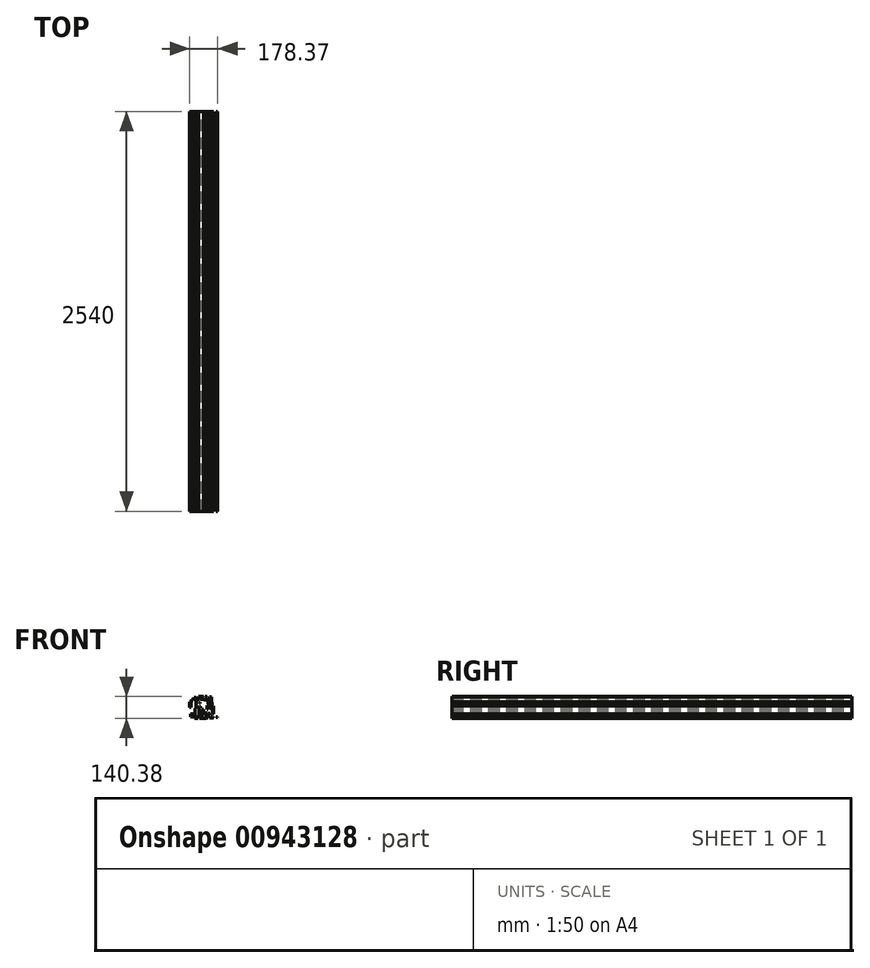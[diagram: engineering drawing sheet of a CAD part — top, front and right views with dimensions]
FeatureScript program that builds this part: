
annotation { "Feature Type Name" : "Feature", "Feature Type Description" : "" }
export const myFeature = defineFeature(function(context is Context, id is Id, definition is map)
    precondition{}
    {
        {
            var Q0;
            Q0=qCreatedBy(makeId("Front.planeOp"),FACE);
            var sketch = newSketch(context, id + "F0", { "sketchPlane" : qUnion([Q0])});
            skLineSegment(sketch, "E0.bottom", {"start": v(-67.4, -14.84) * mm, "end": v(-42.91, -14.84) * mm});
            skLineSegment(sketch, "E0.top", {"start": v(-67.4, -67.62) * mm, "end": v(-42.91, -67.62) * mm});
            skLineSegment(sketch, "E0.left", {"start": v(-67.4, -14.84) * mm, "end": v(-67.4, -67.62) * mm});
            skLineSegment(sketch, "E0.right", {"start": v(-42.91, -14.84) * mm, "end": v(-42.91, -67.62) * mm});
            skLineSegment(sketch, "E1.bottom", {"start": v(9.7, -18.66) * mm, "end": v(14, -18.66) * mm});
            skLineSegment(sketch, "E1.top", {"start": v(9.7, 7.1) * mm, "end": v(14, 7.1) * mm});
            skLineSegment(sketch, "E1.left", {"start": v(9.7, -18.66) * mm, "end": v(9.7, 7.1) * mm});
            skLineSegment(sketch, "E1.right", {"start": v(14, -18.66) * mm, "end": v(14, 7.1) * mm});
            skLineSegment(sketch, "E2.bottom", {"start": v(-19.39, 24.1) * mm, "end": v(-22.09, 24.1) * mm});
            skLineSegment(sketch, "E2.top", {"start": v(-19.39, 24.1) * mm, "end": v(-22.09, 24.1) * mm});
            skLineSegment(sketch, "E2.left", {"start": v(-19.39, 24.1) * mm, "end": v(-19.39, 24.1) * mm});
            skLineSegment(sketch, "E2.right", {"start": v(-22.09, 24.1) * mm, "end": v(-22.09, 24.1) * mm});
            skLineSegment(sketch, "E3.bottom", {"start": v(-36.08, 23.15) * mm, "end": v(-39.73, 23.15) * mm});
            skLineSegment(sketch, "E3.top", {"start": v(-36.08, 17.59) * mm, "end": v(-39.73, 17.59) * mm});
            skLineSegment(sketch, "E3.left", {"start": v(-36.08, 23.15) * mm, "end": v(-36.08, 17.59) * mm});
            skLineSegment(sketch, "E3.right", {"start": v(-39.73, 23.15) * mm, "end": v(-39.73, 17.59) * mm});
            skLineSegment(sketch, "E4.bottom", {"start": v(-38.14, -1.65) * mm, "end": v(-33.7, -1.65) * mm});
            skLineSegment(sketch, "E4.top", {"start": v(-38.14, -9.91) * mm, "end": v(-33.7, -9.91) * mm});
            skLineSegment(sketch, "E4.left", {"start": v(-38.14, -1.65) * mm, "end": v(-38.14, -9.91) * mm});
            skLineSegment(sketch, "E4.right", {"start": v(-33.7, -1.65) * mm, "end": v(-33.7, -9.91) * mm});
            skLineSegment(sketch, "E5.bottom", {"start": v(-27.18, -19.3) * mm, "end": v(-14.3, -19.3) * mm});
            skLineSegment(sketch, "E5.top", {"start": v(-27.18, -38.21) * mm, "end": v(-14.3, -38.21) * mm});
            skLineSegment(sketch, "E5.left", {"start": v(-27.18, -19.3) * mm, "end": v(-27.18, -38.21) * mm});
            skLineSegment(sketch, "E5.right", {"start": v(-14.3, -19.3) * mm, "end": v(-14.3, -38.21) * mm});
            skLineSegment(sketch, "E6.bottom", {"start": v(-6.5, -42.98) * mm, "end": v(7.8, -42.98) * mm});
            skLineSegment(sketch, "E6.top", {"start": v(-6.5, -53.32) * mm, "end": v(7.8, -53.32) * mm});
            skLineSegment(sketch, "E6.left", {"start": v(-6.5, -42.98) * mm, "end": v(-6.5, -53.32) * mm});
            skLineSegment(sketch, "E6.right", {"start": v(7.8, -42.98) * mm, "end": v(7.8, -53.32) * mm});
            skLineSegment(sketch, "E7.bottom", {"start": v(14, -54.59) * mm, "end": v(25.92, -54.59) * mm});
            skLineSegment(sketch, "E7.top", {"start": v(14, -45.53) * mm, "end": v(25.92, -45.53) * mm});
            skLineSegment(sketch, "E7.left", {"start": v(14, -54.59) * mm, "end": v(14, -45.53) * mm});
            skLineSegment(sketch, "E7.right", {"start": v(25.92, -54.59) * mm, "end": v(25.92, -45.53) * mm});
            skLineSegment(sketch, "E8.bottom", {"start": v(33.24, -13.25) * mm, "end": v(26.56, -13.25) * mm});
            skLineSegment(sketch, "E8.top", {"start": v(33.24, 9.96) * mm, "end": v(26.56, 9.96) * mm});
            skLineSegment(sketch, "E8.left", {"start": v(33.24, -13.25) * mm, "end": v(33.24, 9.96) * mm});
            skLineSegment(sketch, "E8.right", {"start": v(26.56, -13.25) * mm, "end": v(26.56, 9.96) * mm});
            skLineSegment(sketch, "E9.bottom", {"start": v(23.86, 16) * mm, "end": v(14.95, 16) * mm});
            skLineSegment(sketch, "E9.top", {"start": v(23.86, 36.67) * mm, "end": v(14.95, 36.67) * mm});
            skLineSegment(sketch, "E9.left", {"start": v(23.86, 16) * mm, "end": v(23.86, 36.67) * mm});
            skLineSegment(sketch, "E9.right", {"start": v(14.95, 16) * mm, "end": v(14.95, 36.67) * mm});
            skLineSegment(sketch, "E10.bottom", {"start": v(11.3, 39.53) * mm, "end": v(-9.53, 39.53) * mm});
            skLineSegment(sketch, "E10.top", {"start": v(11.3, 44.14) * mm, "end": v(-9.53, 44.14) * mm});
            skLineSegment(sketch, "E10.left", {"start": v(11.3, 39.53) * mm, "end": v(11.3, 44.14) * mm});
            skLineSegment(sketch, "E10.right", {"start": v(-9.53, 39.53) * mm, "end": v(-9.53, 44.14) * mm});
            skLineSegment(sketch, "E11.bottom", {"start": v(-12.87, 44.93) * mm, "end": v(-34.33, 44.93) * mm});
            skLineSegment(sketch, "E11.top", {"start": v(-12.87, 46.36) * mm, "end": v(-34.33, 46.36) * mm});
            skLineSegment(sketch, "E11.left", {"start": v(-12.87, 44.93) * mm, "end": v(-12.87, 46.36) * mm});
            skLineSegment(sketch, "E11.right", {"start": v(-34.33, 44.93) * mm, "end": v(-34.33, 46.36) * mm});
            skLineSegment(sketch, "E12.bottom", {"start": v(-42.28, 47.32) * mm, "end": v(-60.88, 47.32) * mm});
            skLineSegment(sketch, "E12.top", {"start": v(-42.28, 39.05) * mm, "end": v(-60.88, 39.05) * mm});
            skLineSegment(sketch, "E12.left", {"start": v(-42.28, 47.32) * mm, "end": v(-42.28, 39.05) * mm});
            skLineSegment(sketch, "E12.right", {"start": v(-60.88, 47.32) * mm, "end": v(-60.88, 39.05) * mm});
            skLineSegment(sketch, "E13.bottom", {"start": v(-63.1, 31.26) * mm, "end": v(-62.95, 31.26) * mm});
            skLineSegment(sketch, "E13.top", {"start": v(-63.1, -2.76) * mm, "end": v(-62.95, -2.76) * mm});
            skLineSegment(sketch, "E13.left", {"start": v(-63.1, 31.26) * mm, "end": v(-63.1, -2.76) * mm});
            skLineSegment(sketch, "E13.right", {"start": v(-62.95, 31.26) * mm, "end": v(-62.95, -2.76) * mm});
            skLineSegment(sketch, "E14.bottom", {"start": v(-62.63, -4.83) * mm, "end": v(-46.73, -4.83) * mm});
            skLineSegment(sketch, "E14.top", {"start": v(-62.63, -20.09) * mm, "end": v(-46.73, -20.09) * mm});
            skLineSegment(sketch, "E14.left", {"start": v(-62.63, -4.83) * mm, "end": v(-62.63, -20.09) * mm});
            skLineSegment(sketch, "E14.right", {"start": v(-46.73, -4.83) * mm, "end": v(-46.73, -20.09) * mm});
            skLineSegment(sketch, "E15.bottom", {"start": v(-37.67, -30.1) * mm, "end": v(-13.5, -30.1) * mm});
            skLineSegment(sketch, "E15.top", {"start": v(-37.67, -54.43) * mm, "end": v(-13.5, -54.43) * mm});
            skLineSegment(sketch, "E15.left", {"start": v(-37.67, -30.1) * mm, "end": v(-37.67, -54.43) * mm});
            skLineSegment(sketch, "E15.right", {"start": v(-13.5, -30.1) * mm, "end": v(-13.5, -54.43) * mm});
            skLineSegment(sketch, "E16.bottom", {"start": v(-2.7, -66.67) * mm, "end": v(15.11, -66.67) * mm});
            skLineSegment(sketch, "E16.top", {"start": v(-2.7, -74.46) * mm, "end": v(15.11, -74.46) * mm});
            skLineSegment(sketch, "E16.left", {"start": v(-2.7, -66.67) * mm, "end": v(-2.7, -74.46) * mm});
            skLineSegment(sketch, "E16.right", {"start": v(15.11, -66.67) * mm, "end": v(15.11, -74.46) * mm});
            skLineSegment(sketch, "E17.bottom", {"start": v(33.08, -74.62) * mm, "end": v(42.93, -74.62) * mm});
            skLineSegment(sketch, "E17.top", {"start": v(33.08, -65.24) * mm, "end": v(42.93, -65.24) * mm});
            skLineSegment(sketch, "E17.left", {"start": v(33.08, -74.62) * mm, "end": v(33.08, -65.24) * mm});
            skLineSegment(sketch, "E17.right", {"start": v(42.93, -74.62) * mm, "end": v(42.93, -65.24) * mm});
            skLineSegment(sketch, "E18.bottom", {"start": v(50.09, -49.5) * mm, "end": v(41.82, -49.5) * mm});
            skLineSegment(sketch, "E18.top", {"start": v(50.09, 2.8) * mm, "end": v(41.82, 2.8) * mm});
            skLineSegment(sketch, "E18.left", {"start": v(50.09, -49.5) * mm, "end": v(50.09, 2.8) * mm});
            skLineSegment(sketch, "E18.right", {"start": v(41.82, -49.5) * mm, "end": v(41.82, 2.8) * mm});
            skLineSegment(sketch, "E19.bottom", {"start": v(40.4, 15.68) * mm, "end": v(38, 15.68) * mm});
            skLineSegment(sketch, "E19.top", {"start": v(40.4, 25.38) * mm, "end": v(38, 25.38) * mm});
            skLineSegment(sketch, "E19.left", {"start": v(40.4, 15.68) * mm, "end": v(40.4, 25.38) * mm});
            skLineSegment(sketch, "E19.right", {"start": v(38, 15.68) * mm, "end": v(38, 25.38) * mm});
            skLineSegment(sketch, "E20.bottom", {"start": v(35.62, 28.4) * mm, "end": v(24.5, 28.4) * mm});
            skLineSegment(sketch, "E20.top", {"start": v(35.62, 60.67) * mm, "end": v(24.5, 60.67) * mm});
            skLineSegment(sketch, "E20.left", {"start": v(35.62, 28.4) * mm, "end": v(35.62, 60.67) * mm});
            skLineSegment(sketch, "E20.right", {"start": v(24.5, 28.4) * mm, "end": v(24.5, 60.67) * mm});
            skLineSegment(sketch, "E21.bottom", {"start": v(7, 60.51) * mm, "end": v(-5.55, 60.51) * mm});
            skLineSegment(sketch, "E21.top", {"start": v(7, 63.06) * mm, "end": v(-5.55, 63.06) * mm});
            skLineSegment(sketch, "E21.left", {"start": v(7, 60.51) * mm, "end": v(7, 63.06) * mm});
            skLineSegment(sketch, "E21.right", {"start": v(-5.55, 60.51) * mm, "end": v(-5.55, 63.06) * mm});
            skLineSegment(sketch, "E22.bottom", {"start": v(-15.25, 61.63) * mm, "end": v(-46.57, 61.63) * mm});
            skLineSegment(sketch, "E22.top", {"start": v(-15.25, 60.2) * mm, "end": v(-46.57, 60.2) * mm});
            skLineSegment(sketch, "E22.left", {"start": v(-15.25, 61.63) * mm, "end": v(-15.25, 60.2) * mm});
            skLineSegment(sketch, "E22.right", {"start": v(-46.57, 61.63) * mm, "end": v(-46.57, 60.2) * mm});
            skLineSegment(sketch, "E23.bottom", {"start": v(-57.38, 60.2) * mm, "end": v(-59.6, 60.2) * mm});
            skLineSegment(sketch, "E23.top", {"start": v(-57.38, 58.92) * mm, "end": v(-59.6, 58.92) * mm});
            skLineSegment(sketch, "E23.left", {"start": v(-57.38, 60.2) * mm, "end": v(-57.38, 58.92) * mm});
            skLineSegment(sketch, "E23.right", {"start": v(-59.6, 60.2) * mm, "end": v(-59.6, 58.92) * mm});
            skLineSegment(sketch, "E24.bottom", {"start": v(-61.36, 57.01) * mm, "end": v(-75.82, 57.01) * mm});
            skLineSegment(sketch, "E24.top", {"start": v(-61.36, 43.82) * mm, "end": v(-75.82, 43.82) * mm});
            skLineSegment(sketch, "E24.left", {"start": v(-61.36, 57.01) * mm, "end": v(-61.36, 43.82) * mm});
            skLineSegment(sketch, "E24.right", {"start": v(-75.82, 57.01) * mm, "end": v(-75.82, 43.82) * mm});
            skLineSegment(sketch, "E25.bottom", {"start": v(-82.02, 43.18) * mm, "end": v(-91.08, 43.18) * mm});
            skLineSegment(sketch, "E25.top", {"start": v(-82.02, 36.35) * mm, "end": v(-91.08, 36.35) * mm});
            skLineSegment(sketch, "E25.left", {"start": v(-82.02, 43.18) * mm, "end": v(-82.02, 36.35) * mm});
            skLineSegment(sketch, "E25.right", {"start": v(-91.08, 43.18) * mm, "end": v(-91.08, 36.35) * mm});
            skLineSegment(sketch, "E26.bottom", {"start": v(-92.52, 28.08) * mm, "end": v(-102.37, 28.08) * mm});
            skLineSegment(sketch, "E26.top", {"start": v(-92.52, -8.33) * mm, "end": v(-102.37, -8.33) * mm});
            skLineSegment(sketch, "E26.left", {"start": v(-92.52, 28.08) * mm, "end": v(-92.52, -8.33) * mm});
            skLineSegment(sketch, "E26.right", {"start": v(-102.37, 28.08) * mm, "end": v(-102.37, -8.33) * mm});
            skLineSegment(sketch, "E27.bottom", {"start": v(-102.69, -12.14) * mm, "end": v(-102.69, -12.14) * mm});
            skLineSegment(sketch, "E27.top", {"start": v(-102.69, -34.4) * mm, "end": v(-102.69, -34.4) * mm});
            skLineSegment(sketch, "E27.left", {"start": v(-102.69, -12.14) * mm, "end": v(-102.69, -34.4) * mm});
            skLineSegment(sketch, "E27.right", {"start": v(-102.69, -12.14) * mm, "end": v(-102.69, -34.4) * mm});
            skLineSegment(sketch, "E28.bottom", {"start": v(-98.24, -47.75) * mm, "end": v(-77.73, -47.75) * mm});
            skLineSegment(sketch, "E28.top", {"start": v(-98.24, -68.26) * mm, "end": v(-77.73, -68.26) * mm});
            skLineSegment(sketch, "E28.left", {"start": v(-98.24, -47.75) * mm, "end": v(-98.24, -68.26) * mm});
            skLineSegment(sketch, "E28.right", {"start": v(-77.73, -47.75) * mm, "end": v(-77.73, -68.26) * mm});
            skLineSegment(sketch, "E29.bottom", {"start": v(-71.69, -70.17) * mm, "end": v(-48.96, -70.17) * mm});
            skLineSegment(sketch, "E29.top", {"start": v(-71.69, -76.37) * mm, "end": v(-48.96, -76.37) * mm});
            skLineSegment(sketch, "E29.left", {"start": v(-71.69, -70.17) * mm, "end": v(-71.69, -76.37) * mm});
            skLineSegment(sketch, "E29.right", {"start": v(-48.96, -70.17) * mm, "end": v(-48.96, -76.37) * mm});
            skLineSegment(sketch, "E30.bottom", {"start": v(-39.9, -77.32) * mm, "end": v(0.96, -77.32) * mm});
            skLineSegment(sketch, "E30.top", {"start": v(-39.9, -76.37) * mm, "end": v(0.96, -76.37) * mm});
            skLineSegment(sketch, "E30.left", {"start": v(-39.9, -77.32) * mm, "end": v(-39.9, -76.37) * mm});
            skLineSegment(sketch, "E30.right", {"start": v(0.96, -77.32) * mm, "end": v(0.96, -76.37) * mm});
            skLineSegment(sketch, "E31.bottom", {"start": v(23.7, -73.35) * mm, "end": v(50.25, -73.35) * mm});
            skLineSegment(sketch, "E31.top", {"start": v(23.7, -72.4) * mm, "end": v(50.25, -72.4) * mm});
            skLineSegment(sketch, "E31.left", {"start": v(23.7, -73.35) * mm, "end": v(23.7, -72.4) * mm});
            skLineSegment(sketch, "E31.right", {"start": v(50.25, -73.35) * mm, "end": v(50.25, -72.4) * mm});
            skLineSegment(sketch, "E32.bottom", {"start": v(65.5, -71.76) * mm, "end": v(76, -71.76) * mm});
            skLineSegment(sketch, "E32.top", {"start": v(65.5, -68.74) * mm, "end": v(76, -68.74) * mm});
            skLineSegment(sketch, "E32.left", {"start": v(65.5, -71.76) * mm, "end": v(65.5, -68.74) * mm});
            skLineSegment(sketch, "E32.right", {"start": v(76, -71.76) * mm, "end": v(76, -68.74) * mm});
            skSolve(sketch);
        }
        {
            var Q0;
            Q0 = qSketchRegion(id + "F0", true);
            extrude(context, id + "F1", {"entities" : qUnion([Q0]), "depth" : 2540 * mm, "offsetDistance" : 25.4 * mm});
        }
    });
